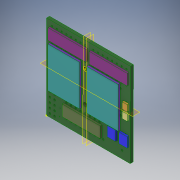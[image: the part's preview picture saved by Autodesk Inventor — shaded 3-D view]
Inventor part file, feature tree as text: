
AUTODESK INVENTOR PART (.ipt)
format: ipt  version: 2019 (Build 230136000, 136)  size: 578,560 bytes
history: native  units: mm
features: other x21, extrude x21, plane x3, sketch x3
ambient origin geometry x8: Origin, YZ Plane, XZ Plane, XY Plane, X Axis, Y Axis, Z Axis, Center Point
bodies: Volumenkörper1 (feature_tree)
feature tree (48):
  other  "NixieModule_IN12.brd"
  extrude  "NixieModule_IN12.brd_Kontur"  Depth=1.0mm TaperAngle=0.0deg
  extrude  "C100_2"  Depth=1.0mm TaperAngle=0.0deg
  extrude  "C101_4"  Depth=1.0mm TaperAngle=0.0deg
  extrude  "C102_6"  Depth=1.0mm TaperAngle=0.0deg
  extrude  "D1_8"  Depth=1.0mm TaperAngle=0.0deg
  extrude  "D2_10"  Depth=1.0mm TaperAngle=0.0deg
  extrude  "GLOW1_12"  Depth=1.0mm TaperAngle=0.0deg
  extrude  "GLOW2_14"  Depth=1.0mm TaperAngle=0.0deg
  extrude  "IC1_16"  Depth=1.0mm TaperAngle=0.0deg
  extrude  "IC2_18"  Depth=1.0mm TaperAngle=0.0deg
  extrude  "IC3_20"  Depth=1.0mm TaperAngle=0.0deg
  extrude  "NIXIE_22"  Depth=1.0mm TaperAngle=0.0deg
  extrude  "R_AN100_24"  Depth=1.0mm TaperAngle=0.0deg
  extrude  "R_AN101_26"  Depth=1.0mm TaperAngle=0.0deg
  extrude  "R_AN_COL100_28"  Depth=1.0mm TaperAngle=0.0deg
  extrude  "R_AN_COL101_30"  Depth=1.0mm TaperAngle=0.0deg
  extrude  "R_BASE_32"  Depth=1.0mm TaperAngle=0.0deg
  extrude  "T1_34"  Depth=1.0mm TaperAngle=0.0deg
  extrude  "T2_36"  Depth=1.0mm TaperAngle=0.0deg
  extrude  "TUBE-1_38"  [1 undecoded]
  extrude  "TUBE-2_40"  [1 undecoded]
  plane  "Arbeitsebene1"
  sketch  "Skizze22"  dims[d4=1.0mm d5=0.0mm d6=1.0mm d7=0.0mm]
  plane  "Arbeitsebene2"
  sketch  "Skizze25"  dims[d8=1.6mm d9=1.0mm d10=0.0mm d11=1.0mm d12=0.0mm d13=1.0mm d14=0.0mm d15=1.0mm d16=0.0mm d17=1.0mm d18=0.0mm d19=1.0mm d20=0.0mm d21=1.0mm d22=0.0mm d23=1.0mm d24=0.0mm d25=1.0mm d26=0.0mm d27=1.0mm d28=0.0mm d29=1.0mm d30=0.0mm d31=1.0mm d32=0.0mm d33=1.0mm d34=0.0mm d35=1.0mm d36=0.0mm d37=1.0mm d38=0.0mm d39=1.0mm d40=0.0mm d41=1.0mm d42=0.0mm]
  plane  "Arbeitsebene4"
  sketch  "Skizze1"  dims[d0=1.6mm d1=0.0mm d2=1.0mm d3=0.0mm]
  other  "C050-024X044, C050-024X044_1"
  other  "C050-024X044, C050-024X044_3"
  other  "C050-024X044, C050-024X044_5"
  other  "WS2812B, SK6812_7"
  other  "WS2812B, SK6812_9"
  other  "LED_LD260, GLOW1_LED_LD260_11"
  other  "LED_LD260, GLOW2_LED_LD260_13"
  other  "DIL16, IC_74141-DIP-16_15"
  other  "DIL16, IC_74141-DIP-16_17"
  other  "DIL16, 74LS595N_19"
  other  "MA06-2, MA06-2_21"
  other  "AXIAL-0_4, R_AN100_AXIAL-0_4_23"
  other  "AXIAL-0_4, R_AN101_AXIAL-0_4_25"
  other  "AXIAL-0_4, R_AN_COL100_AXIAL-0_4_27"
  other  "AXIAL-0_4, R_AN_COL101_AXIAL-0_4_29"
  other  "AXIAL-0_4, R_BASE_AXIAL-0_4_31"
  other  "TO92-EBC, TO92-EBC_33"
  other  "TO92-EBC, TO92-EBC_35"
  other  "IN-12, IN-12A_37"
  other  "IN-12, IN-12A_39"
note: 2 required parameter values undecoded (feature->parameter linkage not recoverable at this tier; creation-order binding heuristic only, values carry confidence <= 0.55)
